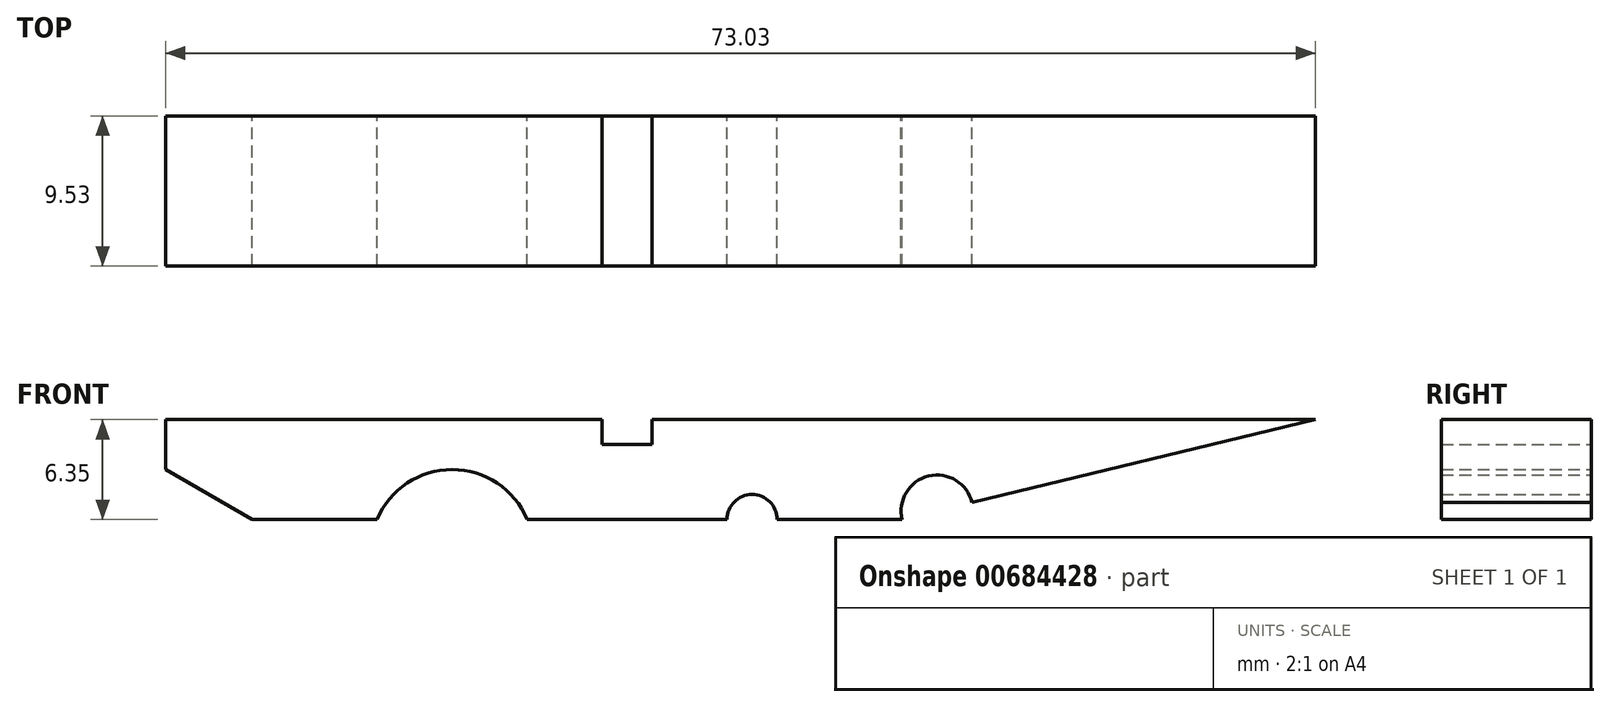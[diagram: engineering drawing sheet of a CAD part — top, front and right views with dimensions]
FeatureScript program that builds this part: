
annotation { "Feature Type Name" : "Feature", "Feature Type Description" : "" }
export const myFeature = defineFeature(function(context is Context, id is Id, definition is map)
    precondition{}
    {
        {
            var Q0;
            Q0=qCreatedBy(makeId("Front.planeOp"),FACE);
            var sketch = newSketch(context, id + "F0", { "sketchPlane" : qUnion([Q0])});
            skLineSegment(sketch, "E0", {"start": v(0, 0) * mm, "end": v(-73.03, 0) * mm});
            skLineSegment(sketch, "E1", {"start": v(-73.03, 0) * mm, "end": v(-73.03, -3.18) * mm});
            skLineSegment(sketch, "E2", {"start": v(-73.03, -3.18) * mm, "end": v(-67.53, -6.35) * mm});
            skLineSegment(sketch, "E3", {"start": v(-67.53, -6.35) * mm, "end": v(-26.25, -6.35) * mm});
            skLineSegment(sketch, "E4", {"start": v(-26.25, -6.35) * mm, "end": v(0, 0) * mm});
            skLineSegment(sketch, "E5", {"start": v(-59.59, -6.35) * mm, "end": v(-50.06, -6.35) * mm});
            skPoint(sketch, "E6.endSnap0", {"position": v(-54.83, -6.35) * mm});
            skArc(sketch, "E7", {"start": v(-50.06, -6.35) * mm, "mid": v(-54.83, -3.17) * mm, "end": v(-59.59, -6.35) * mm});
            skPoint(sketch, "E8.startSnap0", {"position": v(-35.78, -10.84) * mm});
            skArc(sketch, "E9", {"start": v(-34.19, -6.35) * mm, "mid": v(-35.78, -4.76) * mm, "end": v(-37.36, -6.35) * mm});
            skArc(sketch, "E10", {"start": v(-21.8, -5.28) * mm, "mid": v(-24.57, -3.6) * mm, "end": v(-26.25, -6.35) * mm});
            skLineSegment(sketch, "E11", {"start": v(-45.3, -1.59) * mm, "end": v(-45.3, 0) * mm});
            skLineSegment(sketch, "E12", {"start": v(-45.3, -1.59) * mm, "end": v(-42.13, -1.59) * mm});
            skLineSegment(sketch, "E13", {"start": v(-42.13, -1.59) * mm, "end": v(-42.13, 0) * mm});
            skSolve(sketch);
        }
        {
            var Q0;
            {var subQ5=sQuery(id+"F0.wireOp",EDGE,"E0");Q0=makeQuery(id+"F0.imprint","IMPRINT",FACE,{"disambiguationData":[TD([[makeQuery(id+"F0.imprint","IMPRINT",EDGE,{"derivedFrom":subQ5}),1.0]])]});}
            extrude(context, id + "F1", {"entities" : qUnion([Q0]), "depth" : 9.52 * mm, "offsetDistance" : 25.4 * mm});
        }
    });
